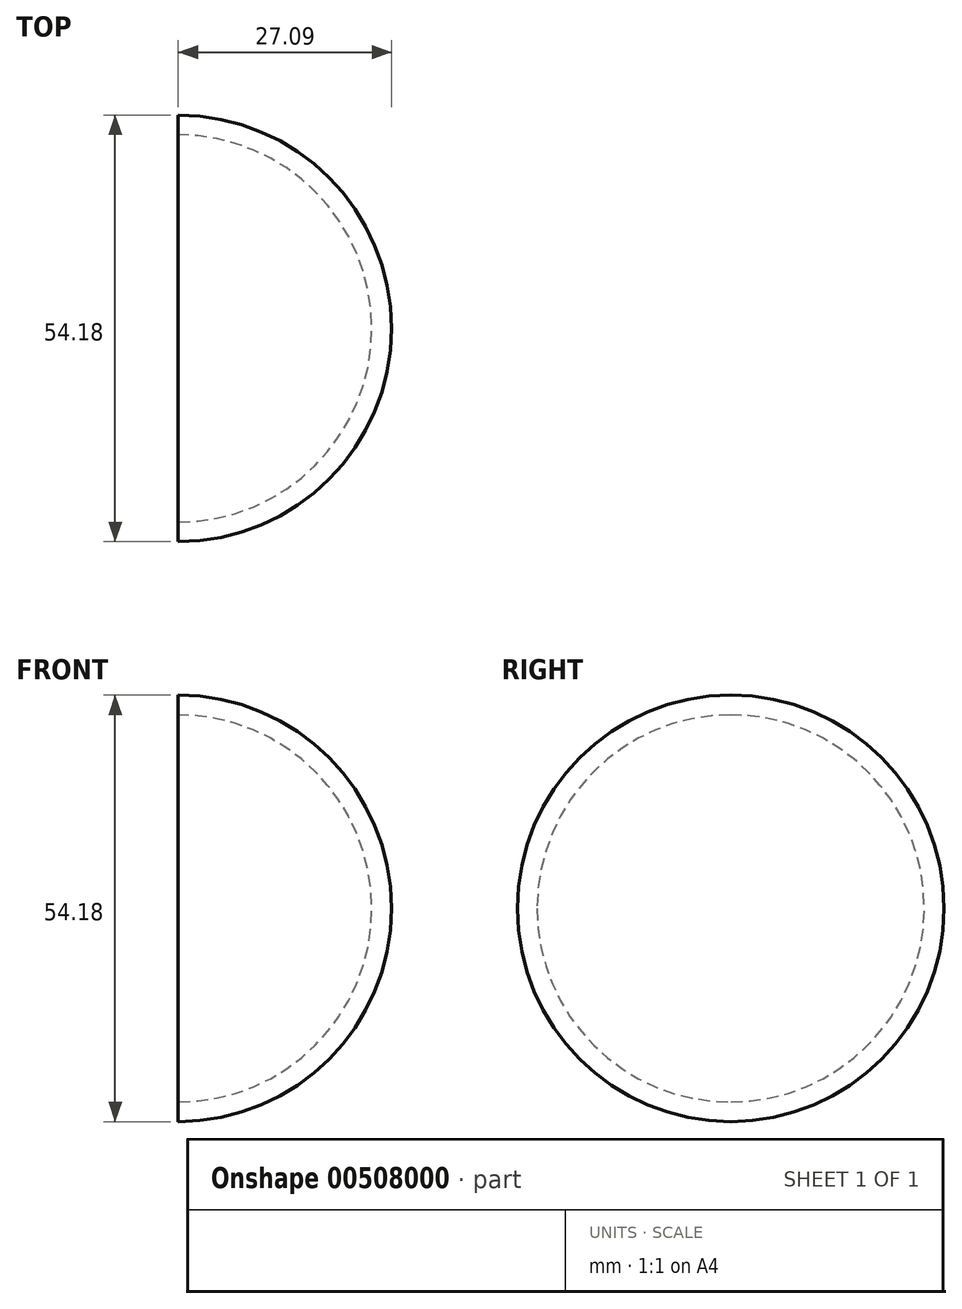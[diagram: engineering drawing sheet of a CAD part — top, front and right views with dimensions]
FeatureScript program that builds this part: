
annotation { "Feature Type Name" : "Feature", "Feature Type Description" : "" }
export const myFeature = defineFeature(function(context is Context, id is Id, definition is map)
    precondition{}
    {
        {
            var Q0;
            Q0=qCreatedBy(makeId("Front.planeOp"),FACE);
            var sketch = newSketch(context, id + "F0", { "sketchPlane" : qUnion([Q0])});
            skArc(sketch, "E0", {"start": v(0, -27.1) * mm, "mid": v(27.1, 0) * mm, "end": v(0, 27.1) * mm});
            skLineSegment(sketch, "E1", {"start": v(0, 27.1) * mm, "end": v(0, -27.1) * mm});
            skSolve(sketch);
        }
        {
            var Q0;
            Q0 = qSketchRegion(id + "F0", true);
            var Q1;
            Q1=sQuery(id+"F0.wireOp",EDGE,"E1");
            revolve(context, id + "F1", {"entities" : qUnion([Q0]), "axis" : qUnion([Q1]), "revolveType" : RevolveType.SYMMETRIC, "angle" : 180 * degree});
        }
        {
            var Q0;
            Q0=makeQuery(id+"F1.opRevolve","CAP_FACE",FACE,{"disambiguationData":[OSD([sQuery(id+"F0.wireOp",EDGE,"E0"),sQuery(id+"F0.wireOp",EDGE,"E1")])],"isStart":true});
            shell(context, id + "F2", {"entities" : qUnion([Q0]), "thickness" : 2.5 * mm});
        }
    });
